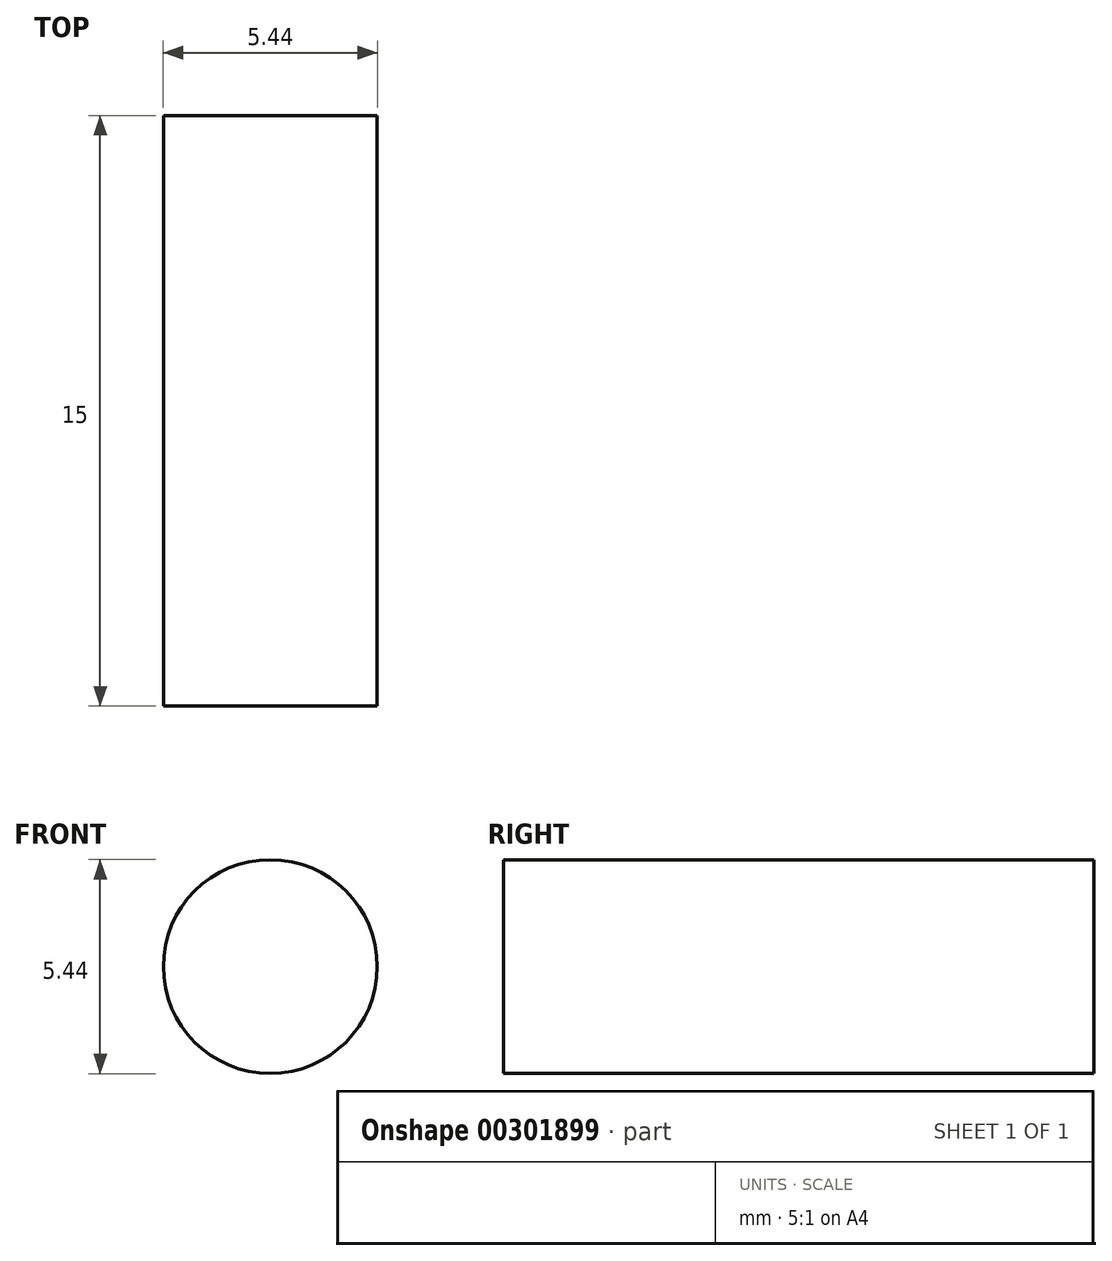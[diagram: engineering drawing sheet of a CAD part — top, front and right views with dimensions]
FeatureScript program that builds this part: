
annotation { "Feature Type Name" : "Feature", "Feature Type Description" : "" }
export const myFeature = defineFeature(function(context is Context, id is Id, definition is map)
    precondition{}
    {
        {
            var Q0;
            Q0=qCreatedBy(makeId("Front.planeOp"),FACE);
            var sketch = newSketch(context, id + "F0", { "sketchPlane" : qUnion([Q0])});
            skCircle(sketch, "E0", {"center": v(0, 0) * mm, "radius": 2.72 * mm});
            skSolve(sketch);
        }
        {
            var Q0;
            Q0 = qSketchRegion(id + "F0", true);
            extrude(context, id + "F1", {"entities" : qUnion([Q0]), "depth" : 15 * mm});
        }
    });
